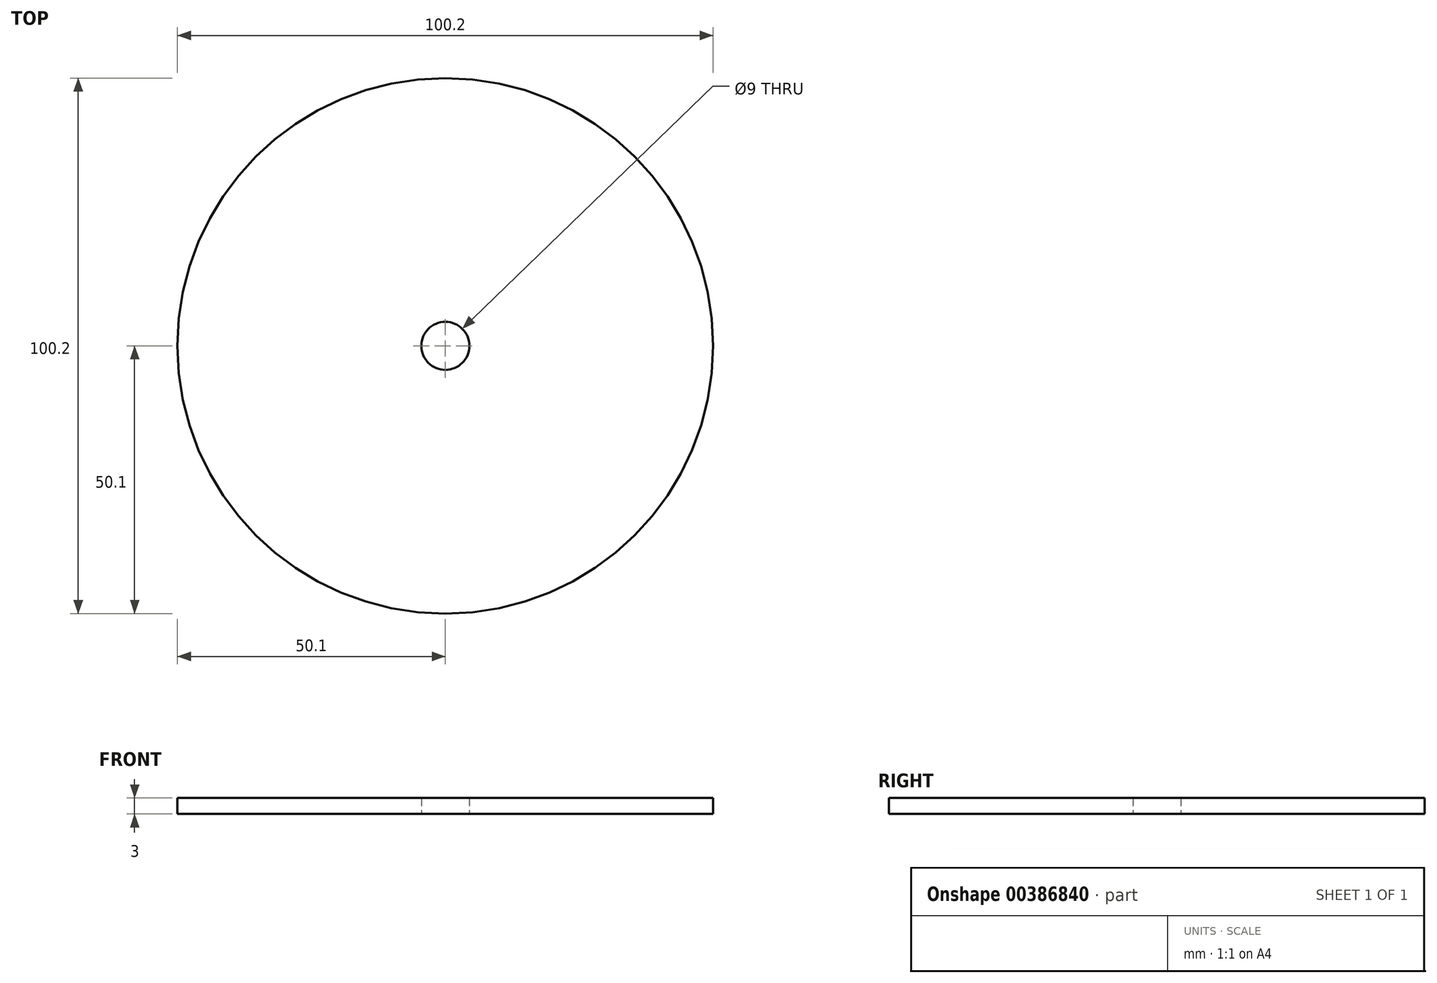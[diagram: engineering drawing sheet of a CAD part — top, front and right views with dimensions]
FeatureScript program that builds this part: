
annotation { "Feature Type Name" : "Feature", "Feature Type Description" : "" }
export const myFeature = defineFeature(function(context is Context, id is Id, definition is map)
    precondition{}
    {
        {
            var Q0;
            Q0=qCreatedBy(makeId("Top.planeOp"),FACE);
            var sketch = newSketch(context, id + "F0", { "sketchPlane" : qUnion([Q0])});
            skCircle(sketch, "E0", {"center": v(0, 0) * mm, "radius": 50.1 * mm});
            skCircle(sketch, "E1", {"center": v(0, 0) * mm, "radius": 4.5 * mm});
            skSolve(sketch);
        }
        {
            var Q0;
            Q0 = qSketchRegion(id + "F0", true);
            extrude(context, id + "F1", {"entities" : qUnion([Q0]), "depth" : 3 * mm});
        }
    });
